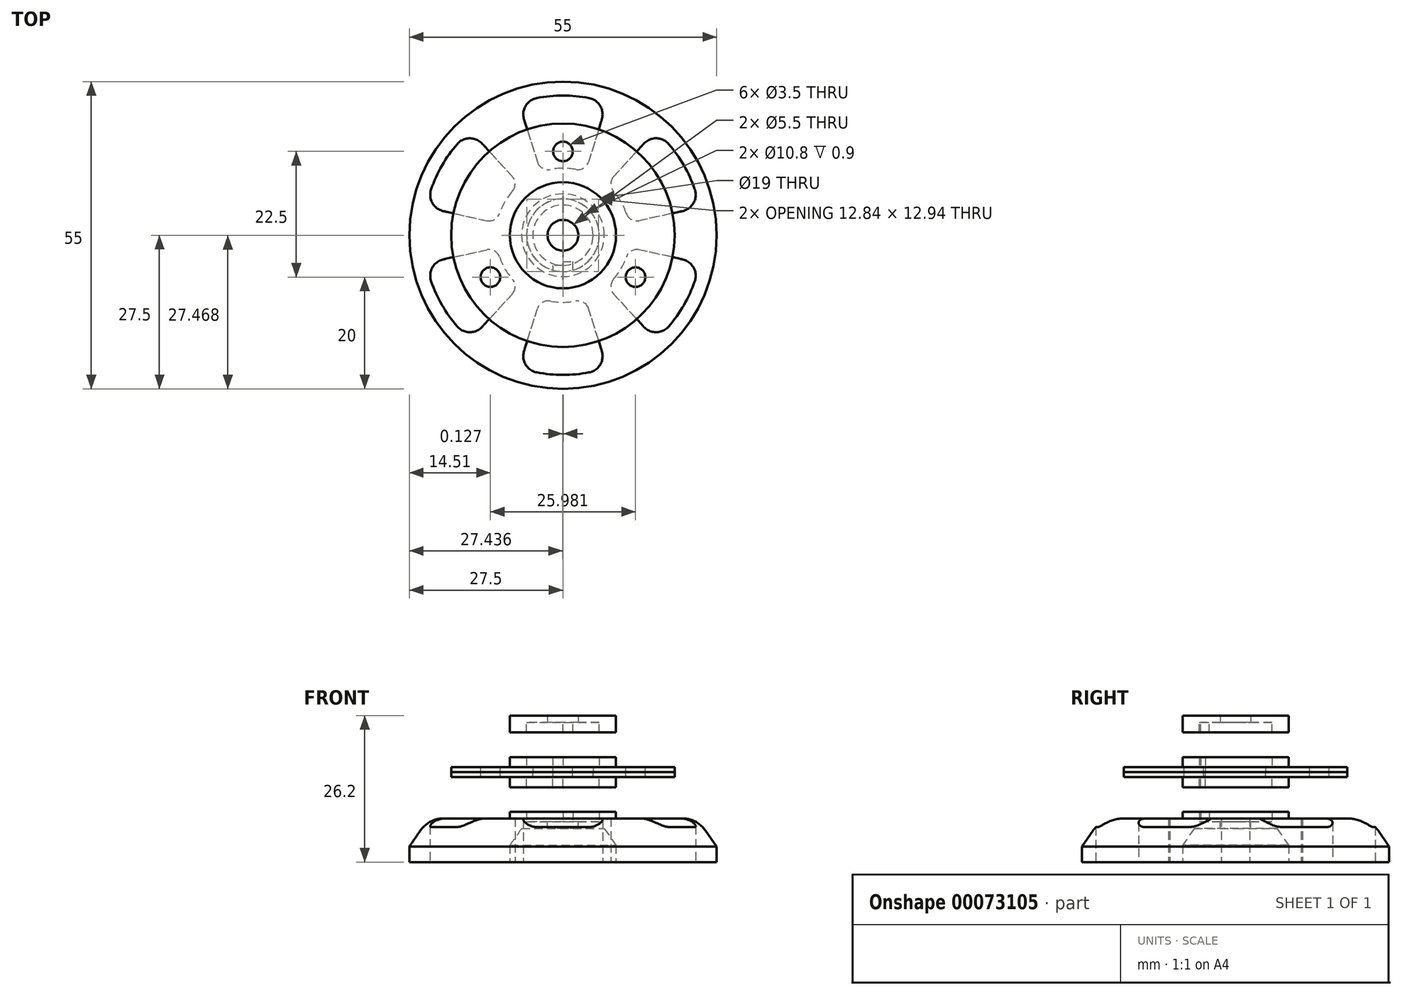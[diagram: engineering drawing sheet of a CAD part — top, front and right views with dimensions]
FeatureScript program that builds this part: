
annotation { "Feature Type Name" : "Feature", "Feature Type Description" : "" }
export const myFeature = defineFeature(function(context is Context, id is Id, definition is map)
    precondition{}
    {
        {
            var Q0;
            Q0=qCreatedBy(makeId("Top.planeOp"),FACE);
            var sketch = newSketch(context, id + "F0", { "sketchPlane" : qUnion([Q0])});
            skCircle(sketch, "E0", {"center": v(0, 0) * mm, "radius": 5.4 * mm});
            skCircle(sketch, "E1", {"center": v(0, 0) * mm, "radius": 20 * mm});
            skSolve(sketch);
        }
        {
            var Q0;
            Q0 = qSketchRegion(id + "F0", true);
            extrude(context, id + "F1", {"entities" : qUnion([Q0]), "depth" : .9 * mm});
        }
        {
            var Q0;
            Q0=makeQuery(id+"F1.opExtrude","CAP_FACE",FACE,{"disambiguationData":[OSD([sQuery(id+"F0.wireOp",EDGE,"E0"),sQuery(id+"F0.wireOp",EDGE,"E1")])],"isStart":false});
            var sketch = newSketch(context, id + "F2", { "sketchPlane" : qUnion([Q0])});
            skCircle(sketch, "E2", {"center": v(0, 0) * mm, "radius": 6.5 * mm});
            skCircle(sketch, "E3", {"center": v(0, 0) * mm, "radius": 9.5 * mm});
            skSolve(sketch);
        }
        {
            var Q0;
            Q0 = qSketchRegion(id + "F2", true);
            extrude(context, id + "F3", {"entities" : qUnion([Q0]), "operationType" : NewBodyOperationType.ADD, "depth" : 1.8 * mm});
        }
        {
            var Q0;
            {var subQ0=sQuery(id+"F0.wireOp",EDGE,"E0");Q0=makeQuery(id+"F3.boolean.opBoolean","SPLIT",FACE,{"disambiguationData":[TD([makeQuery(id+"F1.opExtrude","SWEPT_FACE",FACE,{"disambiguationData":[OSD([subQ0])]})])],"derivedFrom":makeQuery(id+"F1.opExtrude","CAP_FACE",FACE,{"disambiguationData":[OSD([subQ0,sQuery(id+"F0.wireOp",EDGE,"E1")])],"isStart":false})});}
            var sketch = newSketch(context, id + "F4", { "sketchPlane" : qUnion([Q0])});
            skLineSegment(sketch, "E4", {"start": v(0, 0) * mm, "end": v(0, 20) * mm, "construction": true});
            skLineSegment(sketch, "E5.bottom", {"start": v(0, -5.4) * mm, "end": v(-1.8, -5.4) * mm});
            skLineSegment(sketch, "E5.top", {"start": v(0, -7.2) * mm, "end": v(-1.8, -7.2) * mm});
            skLineSegment(sketch, "E5.left", {"start": v(0, -5.4) * mm, "end": v(0, -7.2) * mm});
            skLineSegment(sketch, "E5.right", {"start": v(-1.8, -5.4) * mm, "end": v(-1.8, -7.2) * mm});
            skSolve(sketch);
        }
        {
            var Q0;
            Q0 = qSketchRegion(id + "F4", true);
            var Q1;
            Q1=makeQuery(id+"F3.opExtrude","CAP_FACE",FACE,{"disambiguationData":[OSD([sQuery(id+"F2.wireOp",EDGE,"E2"),sQuery(id+"F2.wireOp",EDGE,"E3")])],"isStart":false});
            extrude(context, id + "F5", {"entities" : qUnion([Q0]), "operationType" : NewBodyOperationType.ADD, "endBound" : BoundingType.UP_TO_SURFACE, "endBoundEntityFace" : qUnion([Q1]), "depth" : 25 * mm});
        }
        {
            var Q0;
            Q0=makeQuery(id+"F1.opExtrude","SWEPT_BODY",BODY,{"disambiguationData":[OSD([sQuery(id+"F0.wireOp",EDGE,"E0"),sQuery(id+"F0.wireOp",EDGE,"E1")])]});
            var Q1;
            Q1=qCreatedBy(makeId("Top.planeOp"),FACE);
            mirror(context, id + "F6", {"entities" : qUnion([Q0]), "mirrorPlane" : qUnion([Q1])});
        }
        {
            var Q0;
            {var subQ0=sQuery(id+"F0.wireOp",EDGE,"E1");Q0=makeQuery(id+"F3.boolean.opBoolean","SPLIT",FACE,{"disambiguationData":[TD([makeQuery(id+"F1.opExtrude","SWEPT_FACE",FACE,{"disambiguationData":[OSD([subQ0])]})])],"derivedFrom":makeQuery(id+"F1.opExtrude","CAP_FACE",FACE,{"disambiguationData":[OSD([sQuery(id+"F0.wireOp",EDGE,"E0"),subQ0])],"isStart":false})});}
            cPlane(context, id + "F7", {"entities" : qUnion([Q0]), "cplaneType" : CPlaneType.OFFSET, "offset" : 8 * mm, "width" : 150 * mm, "height" : 150 * mm});
        }
        {
            var Q0;
            Q0=qCreatedBy(id+"F7.planeOp",FACE);
            var sketch = newSketch(context, id + "F8", { "sketchPlane" : qUnion([Q0])});
            skCircle(sketch, "E6", {"center": v(0, 0) * mm, "radius": 9.5 * mm});
            skCircle(sketch, "E7", {"center": v(0, 0) * mm, "radius": 2.75 * mm});
            skSolve(sketch);
        }
        {
            var Q0;
            Q0 = qSketchRegion(id + "F8", true);
            extrude(context, id + "F9", {"entities" : qUnion([Q0]), "depth" : 1.2 * mm});
        }
        {
            var Q0;
            Q0=makeQuery(id+"F9.opExtrude","CAP_FACE",FACE,{"disambiguationData":[OSD([sQuery(id+"F8.wireOp",EDGE,"E6"),sQuery(id+"F8.wireOp",EDGE,"E7")])],"isStart":true});
            var sketch = newSketch(context, id + "F10", { "sketchPlane" : qUnion([Q0])});
            skCircle(sketch, "E8.0", {"center": v(0, 0) * mm, "radius": 6.5 * mm});
            skCircle(sketch, "E8.1", {"center": v(0, 0) * mm, "radius": 9.5 * mm});
            skSolve(sketch);
        }
        {
            var Q0;
            Q0 = qSketchRegion(id + "F10", true);
            extrude(context, id + "F11", {"entities" : qUnion([Q0]), "operationType" : NewBodyOperationType.ADD, "depth" : 1.8 * mm});
        }
        {
            var Q0;
            Q0=makeQuery(id+"F9.opExtrude","CAP_FACE",FACE,{"disambiguationData":[OSD([sQuery(id+"F8.wireOp",EDGE,"E6"),sQuery(id+"F8.wireOp",EDGE,"E7")])],"isStart":true});
            var sketch = newSketch(context, id + "F12", { "sketchPlane" : qUnion([Q0])});
            skLineSegment(sketch, "E9", {"start": v(0, 0) * mm, "end": v(0, 9.25) * mm, "construction": true});
            skLineSegment(sketch, "E10.bottom", {"start": v(0, 6.5) * mm, "end": v(1.8, 6.5) * mm});
            skLineSegment(sketch, "E10.top", {"start": v(0, 4.7) * mm, "end": v(1.8, 4.7) * mm});
            skLineSegment(sketch, "E10.left", {"start": v(0, 6.5) * mm, "end": v(0, 4.7) * mm});
            skLineSegment(sketch, "E10.right", {"start": v(1.8, 6.5) * mm, "end": v(1.8, 4.7) * mm});
            skSolve(sketch);
        }
        {
            var Q0;
            Q0 = qSketchRegion(id + "F12", true);
            var Q1;
            Q1=makeQuery(id+"F11.opExtrude","CAP_FACE",FACE,{"disambiguationData":[OSD([sQuery(id+"F10.wireOp",EDGE,"E8.0"),sQuery(id+"F10.wireOp",EDGE,"E8.1")])],"isStart":false});
            extrude(context, id + "F13", {"entities" : qUnion([Q0]), "operationType" : NewBodyOperationType.ADD, "endBound" : BoundingType.UP_TO_SURFACE, "endBoundEntityFace" : qUnion([Q1]), "depth" : 1.8 * mm});
        }
        {
            var Q0;
            Q0=makeQuery(id+"F9.opExtrude","SWEPT_BODY",BODY,{"disambiguationData":[OSD([sQuery(id+"F8.wireOp",EDGE,"E6"),sQuery(id+"F8.wireOp",EDGE,"E7")])]});
            var Q1;
            Q1=qCreatedBy(makeId("Top.planeOp"),FACE);
            mirror(context, id + "F14", {"entities" : qUnion([Q0]), "mirrorPlane" : qUnion([Q1])});
        }
        {
            var Q0;
            Q0=makeQuery(id+"F14.opPattern","COPY",FACE,{"derivedFrom":makeQuery(id+"F9.opExtrude","CAP_FACE",FACE,{"disambiguationData":[OSD([sQuery(id+"F8.wireOp",EDGE,"E6"),sQuery(id+"F8.wireOp",EDGE,"E7")])],"isStart":false}),"instanceName":"1"});
            var sketch = newSketch(context, id + "F15", { "sketchPlane" : qUnion([Q0])});
            skCircle(sketch, "E11.0", {"center": v(0, 0) * mm, "radius": 9.5 * mm});
            skCircle(sketch, "E12", {"center": v(0, 0) * mm, "radius": 27.5 * mm});
            skCircle(sketch, "E13", {"center": v(0, 0) * mm, "radius": 12 * mm, "construction": true});
            skCircle(sketch, "E14", {"center": v(0, 0) * mm, "radius": 25 * mm, "construction": true});
            skLineSegment(sketch, "E15", {"start": v(-6.96, 20.71) * mm, "end": v(-4.58, 13.14) * mm});
            skLineSegment(sketch, "E16", {"start": v(0, 0) * mm, "end": v(0, 30.54) * mm, "construction": true});
            skLineSegment(sketch, "E17.MirrorCS", {"start": v(6.96, 20.71) * mm, "end": v(4.58, 13.14) * mm});
            skArc(sketch, "E18", {"start": v(2.29, 11.78) * mm, "mid": v(0, 12) * mm, "end": v(-2.29, 11.78) * mm});
            skArc(sketch, "E19", {"start": v(4.66, 24.56) * mm, "mid": v(0, 25) * mm, "end": v(-4.66, 24.56) * mm});
            skPoint(sketch, "E20.visualSharp", {"position": v(-7.91, 23.72) * mm});
            skArc(sketch, "E20.filletArc", {"start": v(-4.66, 24.56) * mm, "mid": v(-6.68, 23.15) * mm, "end": v(-6.96, 20.71) * mm});
            skPoint(sketch, "E21.visualSharp", {"position": v(7.91, 23.72) * mm});
            skArc(sketch, "E21.filletArc", {"start": v(6.96, 20.71) * mm, "mid": v(6.68, 23.15) * mm, "end": v(4.66, 24.56) * mm});
            skPoint(sketch, "E22.visualSharp", {"position": v(-4, 11.31) * mm});
            skArc(sketch, "E22.filletArc", {"start": v(-4.58, 13.14) * mm, "mid": v(-3.7, 12.02) * mm, "end": v(-2.29, 11.78) * mm});
            skPoint(sketch, "E23.visualSharp", {"position": v(4, 11.31) * mm});
            skArc(sketch, "E23.filletArc", {"start": v(2.29, 11.78) * mm, "mid": v(3.7, 12.02) * mm, "end": v(4.58, 13.14) * mm});
            skArc(sketch, "E24.1.0", {"start": v(-9.06, 7.87) * mm, "mid": v(-10.4, 6) * mm, "end": v(-11.35, 3.9) * mm});
            skLineSegment(sketch, "E24.1.1", {"start": v(-14.46, 16.39) * mm, "end": v(-9.1, 10.53) * mm});
            skLineSegment(sketch, "E24.1.2", {"start": v(-21.42, 4.33) * mm, "end": v(-13.67, 2.6) * mm});
            skArc(sketch, "E24.1.3", {"start": v(-18.94, 16.32) * mm, "mid": v(-21.65, 12.5) * mm, "end": v(-23.6, 8.24) * mm});
            skArc(sketch, "E24.1.4", {"start": v(-23.6, 8.24) * mm, "mid": v(-23.4, 5.8) * mm, "end": v(-21.42, 4.33) * mm});
            skArc(sketch, "E24.1.5", {"start": v(-14.46, 16.39) * mm, "mid": v(-16.71, 17.36) * mm, "end": v(-18.94, 16.32) * mm});
            skPoint(sketch, "E24.1.6", {"position": v(-7.8, 9.12) * mm});
            skPoint(sketch, "E24.1.7", {"position": v(-24.5, 5) * mm});
            skPoint(sketch, "E24.1.8", {"position": v(-16.58, 18.7) * mm});
            skPoint(sketch, "E24.1.9", {"position": v(-11.8, 2.2) * mm});
            skArc(sketch, "E24.1.10", {"start": v(-13.67, 2.6) * mm, "mid": v(-12.26, 2.82) * mm, "end": v(-11.35, 3.9) * mm});
            skArc(sketch, "E24.1.11", {"start": v(-9.06, 7.87) * mm, "mid": v(-8.57, 9.2) * mm, "end": v(-9.1, 10.53) * mm});
            skArc(sketch, "E24.2.0", {"start": v(-11.35, -3.9) * mm, "mid": v(-10.4, -6) * mm, "end": v(-9.06, -7.87) * mm});
            skLineSegment(sketch, "E24.2.1", {"start": v(-21.42, -4.33) * mm, "end": v(-13.67, -2.6) * mm});
            skLineSegment(sketch, "E24.2.2", {"start": v(-14.46, -16.39) * mm, "end": v(-9.1, -10.53) * mm});
            skArc(sketch, "E24.2.3", {"start": v(-23.6, -8.24) * mm, "mid": v(-21.65, -12.5) * mm, "end": v(-18.94, -16.32) * mm});
            skArc(sketch, "E24.2.4", {"start": v(-18.94, -16.32) * mm, "mid": v(-16.71, -17.36) * mm, "end": v(-14.46, -16.39) * mm});
            skArc(sketch, "E24.2.5", {"start": v(-21.42, -4.33) * mm, "mid": v(-23.4, -5.8) * mm, "end": v(-23.6, -8.24) * mm});
            skPoint(sketch, "E24.2.6", {"position": v(-11.8, -2.2) * mm});
            skPoint(sketch, "E24.2.7", {"position": v(-16.58, -18.7) * mm});
            skPoint(sketch, "E24.2.8", {"position": v(-24.5, -5) * mm});
            skPoint(sketch, "E24.2.9", {"position": v(-7.8, -9.12) * mm});
            skArc(sketch, "E24.2.10", {"start": v(-9.1, -10.53) * mm, "mid": v(-8.57, -9.2) * mm, "end": v(-9.06, -7.87) * mm});
            skArc(sketch, "E24.2.11", {"start": v(-11.35, -3.9) * mm, "mid": v(-12.26, -2.82) * mm, "end": v(-13.67, -2.6) * mm});
            skArc(sketch, "E24.3.0", {"start": v(-2.29, -11.78) * mm, "mid": v(0, -12) * mm, "end": v(2.29, -11.78) * mm});
            skLineSegment(sketch, "E24.3.1", {"start": v(-6.96, -20.71) * mm, "end": v(-4.58, -13.14) * mm});
            skLineSegment(sketch, "E24.3.2", {"start": v(6.96, -20.71) * mm, "end": v(4.58, -13.14) * mm});
            skArc(sketch, "E24.3.3", {"start": v(-4.66, -24.56) * mm, "mid": v(0, -25) * mm, "end": v(4.66, -24.56) * mm});
            skArc(sketch, "E24.3.4", {"start": v(4.66, -24.56) * mm, "mid": v(6.68, -23.15) * mm, "end": v(6.96, -20.71) * mm});
            skArc(sketch, "E24.3.5", {"start": v(-6.96, -20.71) * mm, "mid": v(-6.68, -23.15) * mm, "end": v(-4.66, -24.56) * mm});
            skPoint(sketch, "E24.3.6", {"position": v(-4, -11.31) * mm});
            skPoint(sketch, "E24.3.7", {"position": v(7.91, -23.72) * mm});
            skPoint(sketch, "E24.3.8", {"position": v(-7.91, -23.72) * mm});
            skPoint(sketch, "E24.3.9", {"position": v(4, -11.31) * mm});
            skArc(sketch, "E24.3.10", {"start": v(4.58, -13.14) * mm, "mid": v(3.7, -12.02) * mm, "end": v(2.29, -11.78) * mm});
            skArc(sketch, "E24.3.11", {"start": v(-2.29, -11.78) * mm, "mid": v(-3.7, -12.02) * mm, "end": v(-4.58, -13.14) * mm});
            skArc(sketch, "E24.4.0", {"start": v(9.06, -7.87) * mm, "mid": v(10.4, -6) * mm, "end": v(11.35, -3.9) * mm});
            skLineSegment(sketch, "E24.4.1", {"start": v(14.46, -16.39) * mm, "end": v(9.1, -10.53) * mm});
            skLineSegment(sketch, "E24.4.2", {"start": v(21.42, -4.33) * mm, "end": v(13.67, -2.6) * mm});
            skArc(sketch, "E24.4.3", {"start": v(18.94, -16.32) * mm, "mid": v(21.65, -12.5) * mm, "end": v(23.6, -8.24) * mm});
            skArc(sketch, "E24.4.4", {"start": v(23.6, -8.24) * mm, "mid": v(23.4, -5.8) * mm, "end": v(21.42, -4.33) * mm});
            skArc(sketch, "E24.4.5", {"start": v(14.46, -16.39) * mm, "mid": v(16.71, -17.36) * mm, "end": v(18.94, -16.32) * mm});
            skPoint(sketch, "E24.4.6", {"position": v(7.8, -9.12) * mm});
            skPoint(sketch, "E24.4.7", {"position": v(24.5, -5) * mm});
            skPoint(sketch, "E24.4.8", {"position": v(16.58, -18.7) * mm});
            skPoint(sketch, "E24.4.9", {"position": v(11.8, -2.2) * mm});
            skArc(sketch, "E24.4.10", {"start": v(13.67, -2.6) * mm, "mid": v(12.26, -2.82) * mm, "end": v(11.35, -3.9) * mm});
            skArc(sketch, "E24.4.11", {"start": v(9.06, -7.87) * mm, "mid": v(8.57, -9.2) * mm, "end": v(9.1, -10.53) * mm});
            skArc(sketch, "E24.5.0", {"start": v(11.35, 3.9) * mm, "mid": v(10.4, 6) * mm, "end": v(9.06, 7.87) * mm});
            skLineSegment(sketch, "E24.5.1", {"start": v(21.42, 4.33) * mm, "end": v(13.67, 2.6) * mm});
            skLineSegment(sketch, "E24.5.2", {"start": v(14.46, 16.39) * mm, "end": v(9.1, 10.53) * mm});
            skArc(sketch, "E24.5.3", {"start": v(23.6, 8.24) * mm, "mid": v(21.65, 12.5) * mm, "end": v(18.94, 16.32) * mm});
            skArc(sketch, "E24.5.4", {"start": v(18.94, 16.32) * mm, "mid": v(16.71, 17.36) * mm, "end": v(14.46, 16.39) * mm});
            skArc(sketch, "E24.5.5", {"start": v(21.42, 4.33) * mm, "mid": v(23.4, 5.8) * mm, "end": v(23.6, 8.24) * mm});
            skPoint(sketch, "E24.5.6", {"position": v(11.8, 2.2) * mm});
            skPoint(sketch, "E24.5.7", {"position": v(16.58, 18.7) * mm});
            skPoint(sketch, "E24.5.8", {"position": v(24.5, 5) * mm});
            skPoint(sketch, "E24.5.9", {"position": v(7.8, 9.12) * mm});
            skArc(sketch, "E24.5.10", {"start": v(9.1, 10.53) * mm, "mid": v(8.57, 9.2) * mm, "end": v(9.06, 7.87) * mm});
            skArc(sketch, "E24.5.11", {"start": v(11.35, 3.9) * mm, "mid": v(12.26, 2.82) * mm, "end": v(13.67, 2.6) * mm});
            skSolve(sketch);
        }
        {
            var Q0;
            Q0 = qSketchRegion(id + "F15", true);
            extrude(context, id + "F16", {"entities" : qUnion([Q0]), "operationType" : NewBodyOperationType.ADD, "oppositeDirection" : true, "depth" : 1.8 * mm, "hasSecondDirection" : true, "secondDirectionOppositeDirection" : false, "secondDirectionDepth" : 6 * mm});
        }
        {
            var Q0;
            {var subQ0=sQuery(id+"F0.wireOp",EDGE,"E1");Q0=makeQuery(id+"F3.boolean.opBoolean","SPLIT",FACE,{"disambiguationData":[TD([makeQuery(id+"F1.opExtrude","SWEPT_FACE",FACE,{"disambiguationData":[OSD([subQ0])]})])],"derivedFrom":makeQuery(id+"F1.opExtrude","CAP_FACE",FACE,{"disambiguationData":[OSD([sQuery(id+"F0.wireOp",EDGE,"E0"),subQ0])],"isStart":false})});}
            var sketch = newSketch(context, id + "F17", { "sketchPlane" : qUnion([Q0])});
            skLineSegment(sketch, "E25", {"start": v(0, 0) * mm, "end": v(0, 24.26) * mm, "construction": true});
            skCircle(sketch, "E26", {"center": v(0, 15) * mm, "radius": 1.75 * mm});
            skCircle(sketch, "E27.1.0", {"center": v(-13, -7.5) * mm, "radius": 1.75 * mm});
            skCircle(sketch, "E27.2.0", {"center": v(13, -7.5) * mm, "radius": 1.75 * mm});
            skPoint(sketch, "E27.center", {"position": v(0, 0) * mm});
            skSolve(sketch);
        }
        {
            var Q0;
            Q0 = qSketchRegion(id + "F17", true);
            extrude(context, id + "F18", {"entities" : qUnion([Q0]), "operationType" : NewBodyOperationType.REMOVE, "endBound" : BoundingType.THROUGH_ALL, "oppositeDirection" : true, "depth" : 25 * mm});
        }
        {
            var Q0;
            Q0=makeQuery(id+"F16.opExtrude","CAP_EDGE",EDGE,{"disambiguationData":[OSD([sQuery(id+"F15.wireOp",EDGE,"E12")])],"isStart":false});
            chamfer(context, id + "F19", {"entities" : qUnion([Q0]), "chamferType" : ChamferType.OFFSET_ANGLE, "width" : 5 * mm, "oppositeDirection" : false, "angle" : 35 * degree, "tangentPropagation" : true});
        }
        {
            var Q0;
            {var subQ0=sQuery(id+"F15.wireOp",EDGE,"E12");Q0=makeQuery(id+"F19.opChamfer","BLEND_EDGE",EDGE,{"disambiguationData":[OD(0.0)],"blendedFrom":[makeQuery(id+"F16.opExtrude","CAP_EDGE",EDGE,{"disambiguationData":[OSD([subQ0])],"isStart":false}),makeQuery(id+"F16.opExtrude","CAP_FACE",FACE,{"disambiguationData":[OSD([sQuery(id+"F15.wireOp",EDGE,"E11.0"),subQ0,sQuery(id+"F15.wireOp",EDGE,"E15"),sQuery(id+"F15.wireOp",EDGE,"E17.MirrorCS"),sQuery(id+"F15.wireOp",EDGE,"E18"),sQuery(id+"F15.wireOp",EDGE,"E19"),sQuery(id+"F15.wireOp",EDGE,"E20.filletArc"),sQuery(id+"F15.wireOp",EDGE,"E21.filletArc"),sQuery(id+"F15.wireOp",EDGE,"E22.filletArc"),sQuery(id+"F15.wireOp",EDGE,"E23.filletArc"),sQuery(id+"F15.wireOp",EDGE,"E24.1.0"),sQuery(id+"F15.wireOp",EDGE,"E24.1.1"),sQuery(id+"F15.wireOp",EDGE,"E24.1.2"),sQuery(id+"F15.wireOp",EDGE,"E24.1.3"),sQuery(id+"F15.wireOp",EDGE,"E24.1.4"),sQuery(id+"F15.wireOp",EDGE,"E24.1.5"),sQuery(id+"F15.wireOp",EDGE,"E24.1.10"),sQuery(id+"F15.wireOp",EDGE,"E24.1.11"),sQuery(id+"F15.wireOp",EDGE,"E24.2.0"),sQuery(id+"F15.wireOp",EDGE,"E24.2.1"),sQuery(id+"F15.wireOp",EDGE,"E24.2.2"),sQuery(id+"F15.wireOp",EDGE,"E24.2.3"),sQuery(id+"F15.wireOp",EDGE,"E24.2.4"),sQuery(id+"F15.wireOp",EDGE,"E24.2.5"),sQuery(id+"F15.wireOp",EDGE,"E24.2.10"),sQuery(id+"F15.wireOp",EDGE,"E24.2.11"),sQuery(id+"F15.wireOp",EDGE,"E24.3.0"),sQuery(id+"F15.wireOp",EDGE,"E24.3.1"),sQuery(id+"F15.wireOp",EDGE,"E24.3.2"),sQuery(id+"F15.wireOp",EDGE,"E24.3.3"),sQuery(id+"F15.wireOp",EDGE,"E24.3.4"),sQuery(id+"F15.wireOp",EDGE,"E24.3.5"),sQuery(id+"F15.wireOp",EDGE,"E24.3.10"),sQuery(id+"F15.wireOp",EDGE,"E24.3.11"),sQuery(id+"F15.wireOp",EDGE,"E24.4.0"),sQuery(id+"F15.wireOp",EDGE,"E24.4.1"),sQuery(id+"F15.wireOp",EDGE,"E24.4.2"),sQuery(id+"F15.wireOp",EDGE,"E24.4.3"),sQuery(id+"F15.wireOp",EDGE,"E24.4.4"),sQuery(id+"F15.wireOp",EDGE,"E24.4.5"),sQuery(id+"F15.wireOp",EDGE,"E24.4.10"),sQuery(id+"F15.wireOp",EDGE,"E24.4.11"),sQuery(id+"F15.wireOp",EDGE,"E24.5.0"),sQuery(id+"F15.wireOp",EDGE,"E24.5.1"),sQuery(id+"F15.wireOp",EDGE,"E24.5.2"),sQuery(id+"F15.wireOp",EDGE,"E24.5.3"),sQuery(id+"F15.wireOp",EDGE,"E24.5.4"),sQuery(id+"F15.wireOp",EDGE,"E24.5.5"),sQuery(id+"F15.wireOp",EDGE,"E24.5.10"),sQuery(id+"F15.wireOp",EDGE,"E24.5.11")])],"isStart":false})],"blendedInto":[makeQuery(id+"F16.opExtrude","CAP_FACE",FACE,{"disambiguationData":[OSD([sQuery(id+"F15.wireOp",EDGE,"E11.0"),subQ0,sQuery(id+"F15.wireOp",EDGE,"E15"),sQuery(id+"F15.wireOp",EDGE,"E17.MirrorCS"),sQuery(id+"F15.wireOp",EDGE,"E18"),sQuery(id+"F15.wireOp",EDGE,"E19"),sQuery(id+"F15.wireOp",EDGE,"E20.filletArc"),sQuery(id+"F15.wireOp",EDGE,"E21.filletArc"),sQuery(id+"F15.wireOp",EDGE,"E22.filletArc"),sQuery(id+"F15.wireOp",EDGE,"E23.filletArc"),sQuery(id+"F15.wireOp",EDGE,"E24.1.0"),sQuery(id+"F15.wireOp",EDGE,"E24.1.1"),sQuery(id+"F15.wireOp",EDGE,"E24.1.2"),sQuery(id+"F15.wireOp",EDGE,"E24.1.3"),sQuery(id+"F15.wireOp",EDGE,"E24.1.4"),sQuery(id+"F15.wireOp",EDGE,"E24.1.5"),sQuery(id+"F15.wireOp",EDGE,"E24.1.10"),sQuery(id+"F15.wireOp",EDGE,"E24.1.11"),sQuery(id+"F15.wireOp",EDGE,"E24.2.0"),sQuery(id+"F15.wireOp",EDGE,"E24.2.1"),sQuery(id+"F15.wireOp",EDGE,"E24.2.2"),sQuery(id+"F15.wireOp",EDGE,"E24.2.3"),sQuery(id+"F15.wireOp",EDGE,"E24.2.4"),sQuery(id+"F15.wireOp",EDGE,"E24.2.5"),sQuery(id+"F15.wireOp",EDGE,"E24.2.10"),sQuery(id+"F15.wireOp",EDGE,"E24.2.11"),sQuery(id+"F15.wireOp",EDGE,"E24.3.0"),sQuery(id+"F15.wireOp",EDGE,"E24.3.1"),sQuery(id+"F15.wireOp",EDGE,"E24.3.2"),sQuery(id+"F15.wireOp",EDGE,"E24.3.3"),sQuery(id+"F15.wireOp",EDGE,"E24.3.4"),sQuery(id+"F15.wireOp",EDGE,"E24.3.5"),sQuery(id+"F15.wireOp",EDGE,"E24.3.10"),sQuery(id+"F15.wireOp",EDGE,"E24.3.11"),sQuery(id+"F15.wireOp",EDGE,"E24.4.0"),sQuery(id+"F15.wireOp",EDGE,"E24.4.1"),sQuery(id+"F15.wireOp",EDGE,"E24.4.2"),sQuery(id+"F15.wireOp",EDGE,"E24.4.3"),sQuery(id+"F15.wireOp",EDGE,"E24.4.4"),sQuery(id+"F15.wireOp",EDGE,"E24.4.5"),sQuery(id+"F15.wireOp",EDGE,"E24.4.10"),sQuery(id+"F15.wireOp",EDGE,"E24.4.11"),sQuery(id+"F15.wireOp",EDGE,"E24.5.0"),sQuery(id+"F15.wireOp",EDGE,"E24.5.1"),sQuery(id+"F15.wireOp",EDGE,"E24.5.2"),sQuery(id+"F15.wireOp",EDGE,"E24.5.3"),sQuery(id+"F15.wireOp",EDGE,"E24.5.4"),sQuery(id+"F15.wireOp",EDGE,"E24.5.5"),sQuery(id+"F15.wireOp",EDGE,"E24.5.10"),sQuery(id+"F15.wireOp",EDGE,"E24.5.11")])],"isStart":false})]});}
            fillet(context, id + "F20", {"entities" : qUnion([Q0]), "radius" : 5 * mm, "tangentPropagation" : true, "allowEdgeOverflow" : false});
        }
        {
            var Q0;
            Q0=makeQuery(id+"F14.opPattern","COPY",FACE,{"derivedFrom":makeQuery(id+"F9.opExtrude","CAP_FACE",FACE,{"disambiguationData":[OSD([sQuery(id+"F8.wireOp",EDGE,"E6"),sQuery(id+"F8.wireOp",EDGE,"E7")])],"isStart":false}),"instanceName":"1"});
            var sketch = newSketch(context, id + "F21", { "sketchPlane" : qUnion([Q0])});
            skCircle(sketch, "E28.0", {"center": v(0, 0) * mm, "radius": 9.5 * mm});
            skCircle(sketch, "E29", {"center": v(0, 0) * mm, "radius": 5 * mm});
            skSolve(sketch);
        }
        {
            var Q0;
            Q0 = qSketchRegion(id + "F21", true);
            var Q1;
            Q1=makeQuery(id+"F16.opExtrude","CAP_FACE",FACE,{"disambiguationData":[OSD([sQuery(id+"F15.wireOp",EDGE,"E11.0"),sQuery(id+"F15.wireOp",EDGE,"E12"),sQuery(id+"F15.wireOp",EDGE,"E15"),sQuery(id+"F15.wireOp",EDGE,"E17.MirrorCS"),sQuery(id+"F15.wireOp",EDGE,"E18"),sQuery(id+"F15.wireOp",EDGE,"E19"),sQuery(id+"F15.wireOp",EDGE,"E20.filletArc"),sQuery(id+"F15.wireOp",EDGE,"E21.filletArc"),sQuery(id+"F15.wireOp",EDGE,"E22.filletArc"),sQuery(id+"F15.wireOp",EDGE,"E23.filletArc"),sQuery(id+"F15.wireOp",EDGE,"E24.1.0"),sQuery(id+"F15.wireOp",EDGE,"E24.1.1"),sQuery(id+"F15.wireOp",EDGE,"E24.1.2"),sQuery(id+"F15.wireOp",EDGE,"E24.1.3"),sQuery(id+"F15.wireOp",EDGE,"E24.1.4"),sQuery(id+"F15.wireOp",EDGE,"E24.1.5"),sQuery(id+"F15.wireOp",EDGE,"E24.1.10"),sQuery(id+"F15.wireOp",EDGE,"E24.1.11"),sQuery(id+"F15.wireOp",EDGE,"E24.2.0"),sQuery(id+"F15.wireOp",EDGE,"E24.2.1"),sQuery(id+"F15.wireOp",EDGE,"E24.2.2"),sQuery(id+"F15.wireOp",EDGE,"E24.2.3"),sQuery(id+"F15.wireOp",EDGE,"E24.2.4"),sQuery(id+"F15.wireOp",EDGE,"E24.2.5"),sQuery(id+"F15.wireOp",EDGE,"E24.2.10"),sQuery(id+"F15.wireOp",EDGE,"E24.2.11"),sQuery(id+"F15.wireOp",EDGE,"E24.3.0"),sQuery(id+"F15.wireOp",EDGE,"E24.3.1"),sQuery(id+"F15.wireOp",EDGE,"E24.3.2"),sQuery(id+"F15.wireOp",EDGE,"E24.3.3"),sQuery(id+"F15.wireOp",EDGE,"E24.3.4"),sQuery(id+"F15.wireOp",EDGE,"E24.3.5"),sQuery(id+"F15.wireOp",EDGE,"E24.3.10"),sQuery(id+"F15.wireOp",EDGE,"E24.3.11"),sQuery(id+"F15.wireOp",EDGE,"E24.4.0"),sQuery(id+"F15.wireOp",EDGE,"E24.4.1"),sQuery(id+"F15.wireOp",EDGE,"E24.4.2"),sQuery(id+"F15.wireOp",EDGE,"E24.4.3"),sQuery(id+"F15.wireOp",EDGE,"E24.4.4"),sQuery(id+"F15.wireOp",EDGE,"E24.4.5"),sQuery(id+"F15.wireOp",EDGE,"E24.4.10"),sQuery(id+"F15.wireOp",EDGE,"E24.4.11"),sQuery(id+"F15.wireOp",EDGE,"E24.5.0"),sQuery(id+"F15.wireOp",EDGE,"E24.5.1"),sQuery(id+"F15.wireOp",EDGE,"E24.5.2"),sQuery(id+"F15.wireOp",EDGE,"E24.5.3"),sQuery(id+"F15.wireOp",EDGE,"E24.5.4"),sQuery(id+"F15.wireOp",EDGE,"E24.5.5"),sQuery(id+"F15.wireOp",EDGE,"E24.5.10"),sQuery(id+"F15.wireOp",EDGE,"E24.5.11")])],"isStart":true});
            extrude(context, id + "F22", {"entities" : qUnion([Q0]), "operationType" : NewBodyOperationType.ADD, "endBound" : BoundingType.UP_TO_SURFACE, "endBoundEntityFace" : qUnion([Q1]), "depth" : 25 * mm});
        }
        {
            var Q0;
            Q0=makeQuery(id+"F22.boolean.opBoolean","MERGE",FACE,{"derivedFrom":[makeQuery(id+"F16.opExtrude","CAP_FACE",FACE,{"disambiguationData":[OSD([sQuery(id+"F15.wireOp",EDGE,"E11.0"),sQuery(id+"F15.wireOp",EDGE,"E12"),sQuery(id+"F15.wireOp",EDGE,"E15"),sQuery(id+"F15.wireOp",EDGE,"E17.MirrorCS"),sQuery(id+"F15.wireOp",EDGE,"E18"),sQuery(id+"F15.wireOp",EDGE,"E19"),sQuery(id+"F15.wireOp",EDGE,"E20.filletArc"),sQuery(id+"F15.wireOp",EDGE,"E21.filletArc"),sQuery(id+"F15.wireOp",EDGE,"E22.filletArc"),sQuery(id+"F15.wireOp",EDGE,"E23.filletArc"),sQuery(id+"F15.wireOp",EDGE,"E24.1.0"),sQuery(id+"F15.wireOp",EDGE,"E24.1.1"),sQuery(id+"F15.wireOp",EDGE,"E24.1.2"),sQuery(id+"F15.wireOp",EDGE,"E24.1.3"),sQuery(id+"F15.wireOp",EDGE,"E24.1.4"),sQuery(id+"F15.wireOp",EDGE,"E24.1.5"),sQuery(id+"F15.wireOp",EDGE,"E24.1.10"),sQuery(id+"F15.wireOp",EDGE,"E24.1.11"),sQuery(id+"F15.wireOp",EDGE,"E24.2.0"),sQuery(id+"F15.wireOp",EDGE,"E24.2.1"),sQuery(id+"F15.wireOp",EDGE,"E24.2.2"),sQuery(id+"F15.wireOp",EDGE,"E24.2.3"),sQuery(id+"F15.wireOp",EDGE,"E24.2.4"),sQuery(id+"F15.wireOp",EDGE,"E24.2.5"),sQuery(id+"F15.wireOp",EDGE,"E24.2.10"),sQuery(id+"F15.wireOp",EDGE,"E24.2.11"),sQuery(id+"F15.wireOp",EDGE,"E24.3.0"),sQuery(id+"F15.wireOp",EDGE,"E24.3.1"),sQuery(id+"F15.wireOp",EDGE,"E24.3.2"),sQuery(id+"F15.wireOp",EDGE,"E24.3.3"),sQuery(id+"F15.wireOp",EDGE,"E24.3.4"),sQuery(id+"F15.wireOp",EDGE,"E24.3.5"),sQuery(id+"F15.wireOp",EDGE,"E24.3.10"),sQuery(id+"F15.wireOp",EDGE,"E24.3.11"),sQuery(id+"F15.wireOp",EDGE,"E24.4.0"),sQuery(id+"F15.wireOp",EDGE,"E24.4.1"),sQuery(id+"F15.wireOp",EDGE,"E24.4.2"),sQuery(id+"F15.wireOp",EDGE,"E24.4.3"),sQuery(id+"F15.wireOp",EDGE,"E24.4.4"),sQuery(id+"F15.wireOp",EDGE,"E24.4.5"),sQuery(id+"F15.wireOp",EDGE,"E24.4.10"),sQuery(id+"F15.wireOp",EDGE,"E24.4.11"),sQuery(id+"F15.wireOp",EDGE,"E24.5.0"),sQuery(id+"F15.wireOp",EDGE,"E24.5.1"),sQuery(id+"F15.wireOp",EDGE,"E24.5.2"),sQuery(id+"F15.wireOp",EDGE,"E24.5.3"),sQuery(id+"F15.wireOp",EDGE,"E24.5.4"),sQuery(id+"F15.wireOp",EDGE,"E24.5.5"),sQuery(id+"F15.wireOp",EDGE,"E24.5.10"),sQuery(id+"F15.wireOp",EDGE,"E24.5.11")])],"isStart":true}),makeQuery(id+"F22.opExtrude","CAP_FACE",FACE,{"disambiguationData":[OSD([sQuery(id+"F21.wireOp",EDGE,"E28.0"),sQuery(id+"F21.wireOp",EDGE,"E29")])],"isStart":false})]});
            var sketch = newSketch(context, id + "F23", { "sketchPlane" : qUnion([Q0])});
            skCircle(sketch, "E30", {"center": v(0, 0) * mm, "radius": 9.5 * mm});
            skSolve(sketch);
        }
        {
            var Q0;
            Q0 = qSketchRegion(id + "F23", true);
            var Q1;
            Q1=makeQuery(id+"F14.opPattern","COPY",FACE,{"derivedFrom":makeQuery(id+"F9.opExtrude","CAP_FACE",FACE,{"disambiguationData":[OSD([sQuery(id+"F8.wireOp",EDGE,"E6"),sQuery(id+"F8.wireOp",EDGE,"E7")])],"isStart":false}),"instanceName":"1"});
            extrude(context, id + "F24", {"entities" : qUnion([Q0]), "operationType" : NewBodyOperationType.REMOVE, "endBound" : BoundingType.UP_TO_SURFACE, "oppositeDirection" : true, "endBoundEntityFace" : qUnion([Q1]), "depth" : 25 * mm});
        }
        {
            var Q0;
            Q0=makeQuery(id+"F24.boolean.opBoolean","COPY",EDGE,{"derivedFrom":makeQuery(id+"F24.opExtrude","CAP_EDGE",EDGE,{"disambiguationData":[OSD([sQuery(id+"F23.wireOp",EDGE,"E30")])],"isStart":false})});
            chamfer(context, id + "F25", {"entities" : qUnion([Q0]), "chamferType" : ChamferType.OFFSET_ANGLE, "width" : 3 * mm, "oppositeDirection" : false, "angle" : 35 * degree, "tangentPropagation" : true});
        }
    });
